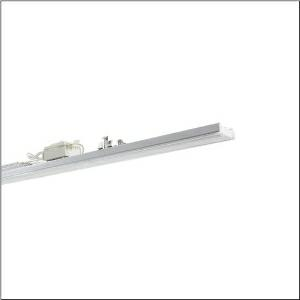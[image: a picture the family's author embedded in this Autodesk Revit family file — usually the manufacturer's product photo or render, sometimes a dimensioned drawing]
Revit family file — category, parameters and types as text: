
# Revit family: licross_r__11_recessed_mo_51tl19cn485g_7cda
name_source: partatom
category: Lighting Fixtures
units: mm (PartAtom-declared; Revit-internal decimal feet)

## family parameters
Cut with Voids When Loaded = No
Host = Face
Light Source = No
Part Type = Normal
Room Calculation Point = No
Round Connector Dimension = Use Diameter
Shared = No

## types (1)
- --- (1 x LED, 8920 lm, 49.3 W, 4000K)
    Apparent Load = 49 VA
    CIE Flux Codes = 55 90 98 100 100
    Color Rendering = 80
    Color Temperature = 4000K
    Default Elevation = 1800 mm
    Description = Licross® 11 Recessed MO, luminaire insert, of sheet steel, coil coated, white, length: 1.500mm, width: 66mm, height: 67mm, LED rated luminous flux: 8.920lm, light colour: 840, control gear: ON/OFF Multilumen, CLOi, with plug, 3-pole, with phase selection, mains connection: 220..240V, AC, 50/60Hz, start of lifetime: 49W, end of service life: 55W, internal wiring halogen-free, primary light control with lens, of plastic, primary optical cover: cover, of PMMA, light emission: direct distribution, primary light characteristic: double asymmetric, protection rating (complete): IP40, insulation class (complete): insulation class I (protective earthing), certification: CE, ENEC, VDE, UKCA, protection symbol: D if used in an environment without relevant dust loads with corresponding accessories, impact resistance: IK06, permissible ambient temperature for indoor applications: -35..+40°C, corresponds to IFS (International Featured Standards) requirements for safety and quality in the food industry, reducing of maximum allowable ambient temperature of 5°C with ceiling mounting, LABS conformity tested according to VDMA 24364:2018-05, packaging unit: 1 piece
    Height = 58 mm
    Lamp = 1 x LED
    Lamp Light Flux = 8920 lm
    Lamp Power = 49.3 W
    Lamp count = 1
    Length = 1500 mm
    Luminous efficacy = 181 lm/W
    Manufacturer = Siteco
    ModVariant = No
    Model = 51TL19CN485G
    Mounting Place = Ceiling
    Mounting Type = Pendant
    Number of Poles = 1
    OnlyDefault = Yes
    Power Factor = 1
    Product Name = Licross® 11 Recessed MO
    Product group = luminaire insert | ceiling pendant
    ProductGroupID = 902
    Protection Class = Protection class I
    Protection Degree = IP 40
    RLX_Detail_Level = 1
    RLX_Emergency_Light_Flux = 0 lm
    RLX_Emergency_Type = 0
    RLX_Emergency_Type_DB = No
    RlxData = <blob elided: 22377 chars, md5=fd5cca6d>
    Socket = socket
    Standby Power = 0 W
    System Light Flux = 8920 lm
    System Power = 49 W
    Type Comments = factory setting: luminous flux: 100 % | (A | C | E) | 113 mA
    Type Image = l_1296930.jpg
    URL = http://relux.com
    VarID = @adj_107141
    Voltage = 0 V
    Weight = 0.00 kg
    Width = 66 mm

## geometry (parser evidence)
native form markers: Blend x4, Sweep x11
no freeform markers — native parametric forms only
